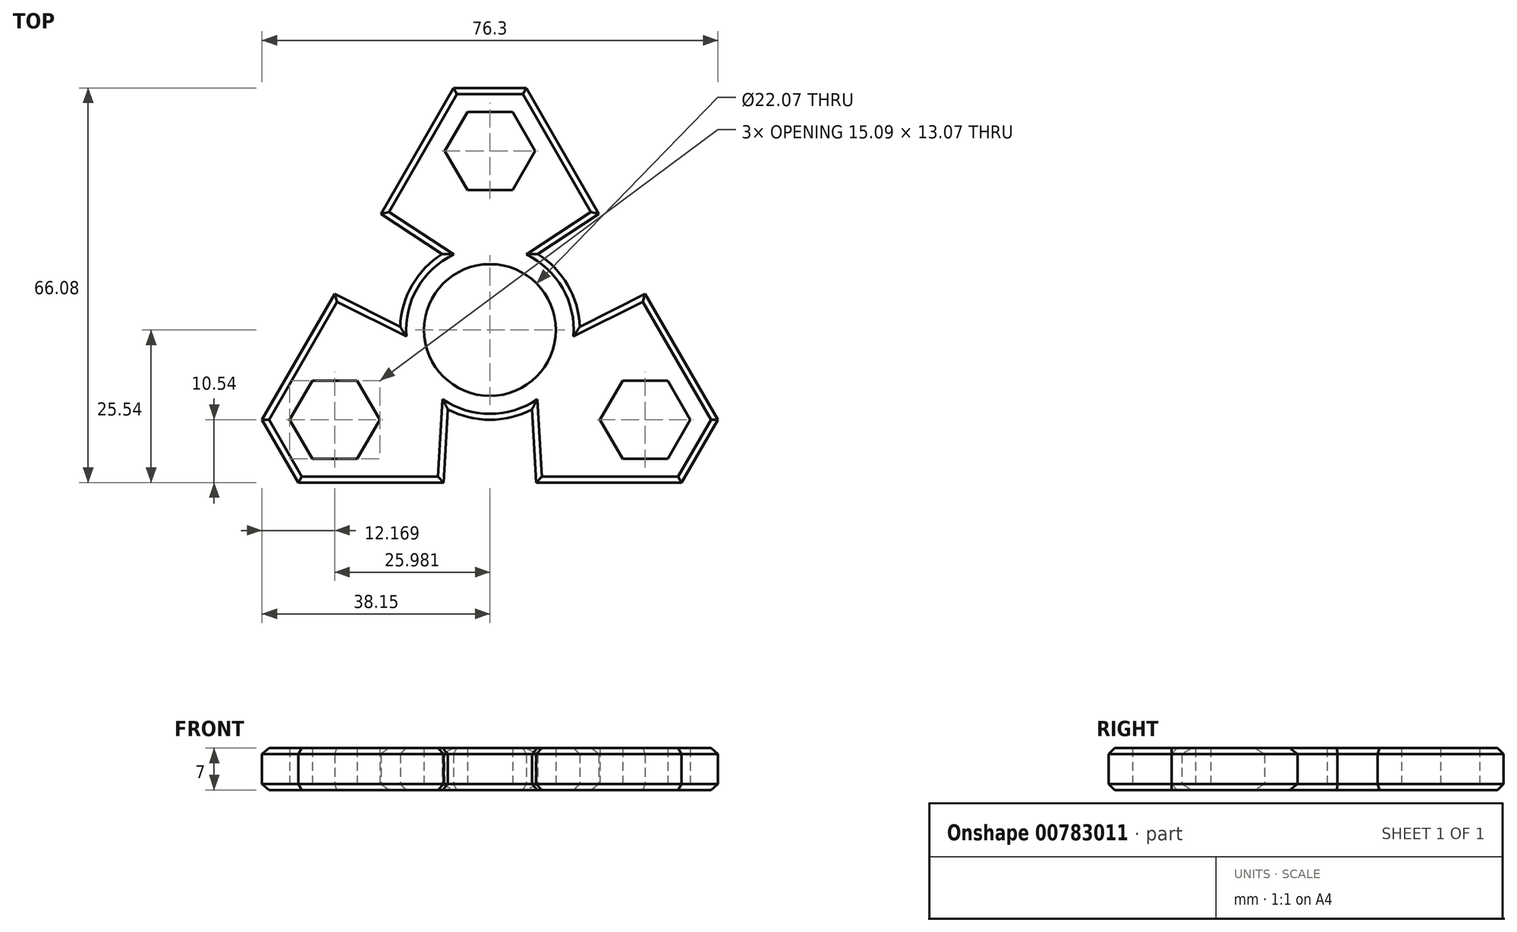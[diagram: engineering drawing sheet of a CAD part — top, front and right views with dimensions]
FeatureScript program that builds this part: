
annotation { "Feature Type Name" : "Feature", "Feature Type Description" : "" }
export const myFeature = defineFeature(function(context is Context, id is Id, definition is map)
    precondition{}
    {
        {
            var Q0;
            Q0=qCreatedBy(makeId("Top.planeOp"),FACE);
            var sketch = newSketch(context, id + "F0", { "sketchPlane" : qUnion([Q0])});
            skCircle(sketch, "E0", {"center": v(0, 0) * mm, "radius": 11.04 * mm});
            skCircle(sketch, "E1", {"center": v(0, 0) * mm, "radius": 15.04 * mm});
            skLineSegment(sketch, "E2", {"start": v(0, 0) * mm, "end": v(0, 79.85) * mm, "construction": true});
            skCircle(sketch, "E3.cCircle", {"center": v(0, 30) * mm, "radius": 6.53 * mm, "construction": true});
            skLineSegment(sketch, "E3.0", {"start": v(3.77, 23.46) * mm, "end": v(-3.77, 23.46) * mm});
            skLineSegment(sketch, "E3.1", {"start": v(-3.77, 23.46) * mm, "end": v(-7.55, 30) * mm});
            skLineSegment(sketch, "E3.2", {"start": v(-7.55, 30) * mm, "end": v(-3.77, 36.53) * mm});
            skLineSegment(sketch, "E3.3", {"start": v(-3.77, 36.53) * mm, "end": v(3.77, 36.53) * mm});
            skLineSegment(sketch, "E3.4", {"start": v(3.77, 36.53) * mm, "end": v(7.55, 30) * mm});
            skLineSegment(sketch, "E3.5", {"start": v(7.55, 30) * mm, "end": v(3.77, 23.46) * mm});
            skPoint(sketch, "E3.0.midPoint", {"position": v(0, 23.46) * mm});
            skCircle(sketch, "E4.cCircle", {"center": v(0, 30) * mm, "radius": 10.54 * mm, "construction": true});
            skLineSegment(sketch, "E4.0", {"start": v(6.08, 19.46) * mm, "end": v(-6.08, 19.46) * mm});
            skLineSegment(sketch, "E4.1", {"start": v(-6.08, 19.46) * mm, "end": v(-12.16, 30) * mm});
            skLineSegment(sketch, "E4.2", {"start": v(-12.16, 30) * mm, "end": v(-6.08, 40.53) * mm});
            skLineSegment(sketch, "E4.3", {"start": v(-6.08, 40.53) * mm, "end": v(6.08, 40.53) * mm});
            skLineSegment(sketch, "E4.4", {"start": v(6.08, 40.54) * mm, "end": v(12.16, 30) * mm});
            skLineSegment(sketch, "E4.5", {"start": v(12.16, 30) * mm, "end": v(6.08, 19.46) * mm});
            skPoint(sketch, "E4.0.midPoint", {"position": v(0, 19.46) * mm});
            skLineSegment(sketch, "E5", {"start": v(12.16, 30) * mm, "end": v(18.25, 19.46) * mm});
            skLineSegment(sketch, "E6", {"start": v(18.25, 19.47) * mm, "end": v(8, 12.73) * mm});
            skLineSegment(sketch, "E7", {"start": v(-12.16, 30) * mm, "end": v(-18.25, 19.46) * mm});
            skLineSegment(sketch, "E8", {"start": v(-18.25, 19.46) * mm, "end": v(-8, 12.73) * mm});
            skCircle(sketch, "E9", {"center": v(0, 0) * mm, "radius": 40.99 * mm, "construction": true});
            skLineSegment(sketch, "E10", {"start": v(0, 12.73) * mm, "end": v(8, 12.73) * mm, "construction": true});
            skLineSegment(sketch, "E11", {"start": v(0, 12.73) * mm, "end": v(-8, 12.73) * mm, "construction": true});
            skSolve(sketch);
        }
        {
            var Q0;
            Q0=qCreatedBy(makeId("Right.planeOp"),FACE);
            var sketch = newSketch(context, id + "F1", { "sketchPlane" : qUnion([Q0])});
            skLineSegment(sketch, "E12", {"start": v(0, 0) * mm, "end": v(0, 65.4) * mm, "construction": true});
            skSolve(sketch);
        }
        {
            var Q0;
            Q0=makeQuery(id+"F0.imprint","IMPRINT",FACE,{"disambiguationData":[TD([[makeQuery(id+"F0.imprint","IMPRINT",EDGE,{"derivedFrom":sQuery(id+"F0.wireOp",EDGE,"E0")}),-1.0]])]});
            var Q1;
            Q1=makeQuery(id+"F0.imprint","IMPRINT",FACE,{"disambiguationData":[TD([[makeQuery(id+"F0.imprint","IMPRINT",EDGE,{"derivedFrom":sQuery(id+"F0.wireOp",EDGE,"E3.0")}),1.0]])]});
            var Q2;
            Q2=makeQuery(id+"F0.imprint","IMPRINT",FACE,{"disambiguationData":[TD([[makeQuery(id+"F0.imprint","IMPRINT",EDGE,{"derivedFrom":sQuery(id+"F0.wireOp",EDGE,"E4.0")}),1.0]])]});
            var Q3;
            Q3=makeQuery(id+"F0.imprint","IMPRINT",FACE,{"disambiguationData":[TD([[makeQuery(id+"F0.imprint","IMPRINT",EDGE,{"derivedFrom":sQuery(id+"F0.wireOp",EDGE,"E4.2")}),1.0]])]});
            extrude(context, id + "F2", {"entities" : qUnion([Q0, Q1, Q2, Q3]), "depth" : 7 * mm, "offsetDistance" : 25 * mm});
        }
        {
            var Q0;
            Q0=makeQuery(id+"F2.opExtrude","CAP_EDGE",EDGE,{"disambiguationData":[OSD([sQuery(id+"F0.wireOp",EDGE,"E4.4"),sQuery(id+"F0.wireOp",EDGE,"E5")])],"isStart":false});
            var Q1;
            Q1=makeQuery(id+"F2.opExtrude","CAP_EDGE",EDGE,{"disambiguationData":[OSD([sQuery(id+"F0.wireOp",EDGE,"E4.3")])],"isStart":false});
            var Q2;
            Q2=makeQuery(id+"F2.opExtrude","CAP_EDGE",EDGE,{"disambiguationData":[OSD([sQuery(id+"F0.wireOp",EDGE,"E4.2"),sQuery(id+"F0.wireOp",EDGE,"E7")])],"isStart":true});
            var Q3;
            Q3=makeQuery(id+"F2.opExtrude","CAP_EDGE",EDGE,{"disambiguationData":[OSD([sQuery(id+"F0.wireOp",EDGE,"E6")])],"isStart":false});
            var Q4;
            Q4=makeQuery(id+"F2.opExtrude","CAP_EDGE",EDGE,{"disambiguationData":[OSD([sQuery(id+"F0.wireOp",EDGE,"E8")])],"isStart":false});
            var Q5;
            Q5=makeQuery(id+"F2.opExtrude","CAP_EDGE",EDGE,{"disambiguationData":[OSD([sQuery(id+"F0.wireOp",EDGE,"E6")])],"isStart":true});
            var Q6;
            Q6=makeQuery(id+"F2.opExtrude","CAP_EDGE",EDGE,{"disambiguationData":[OSD([sQuery(id+"F0.wireOp",EDGE,"E4.4"),sQuery(id+"F0.wireOp",EDGE,"E5")])],"isStart":true});
            var Q7;
            Q7=makeQuery(id+"F2.opExtrude","CAP_EDGE",EDGE,{"disambiguationData":[OSD([sQuery(id+"F0.wireOp",EDGE,"E4.3")])],"isStart":true});
            var Q8;
            Q8=makeQuery(id+"F2.opExtrude","CAP_EDGE",EDGE,{"disambiguationData":[OSD([sQuery(id+"F0.wireOp",EDGE,"E4.2"),sQuery(id+"F0.wireOp",EDGE,"E7")])],"isStart":false});
            var Q9;
            Q9=makeQuery(id+"F2.opExtrude","CAP_EDGE",EDGE,{"disambiguationData":[OSD([sQuery(id+"F0.wireOp",EDGE,"E1")])],"isStart":true});
            var Q10;
            Q10=makeQuery(id+"F2.opExtrude","CAP_EDGE",EDGE,{"disambiguationData":[OSD([sQuery(id+"F0.wireOp",EDGE,"E1")])],"isStart":false});
            var Q11;
            Q11=makeQuery(id+"F2.opExtrude","CAP_EDGE",EDGE,{"disambiguationData":[OSD([sQuery(id+"F0.wireOp",EDGE,"E8")])],"isStart":true});
            chamfer(context, id + "F3", {"entities" : qUnion([Q0, Q1, Q2, Q3, Q4, Q5, Q6, Q7, Q8, Q9, Q10, Q11]), "width" : 1 * mm, "tangentPropagation" : true});
        }
        {
            var Q0;
            Q0=makeQuery(id+"F2.opExtrude","SWEPT_BODY",BODY,{"disambiguationData":[OSD([sQuery(id+"F0.wireOp",EDGE,"E0"),sQuery(id+"F0.wireOp",EDGE,"E1"),sQuery(id+"F0.wireOp",EDGE,"E3.0"),sQuery(id+"F0.wireOp",EDGE,"E3.1"),sQuery(id+"F0.wireOp",EDGE,"E3.2"),sQuery(id+"F0.wireOp",EDGE,"E3.3"),sQuery(id+"F0.wireOp",EDGE,"E3.4"),sQuery(id+"F0.wireOp",EDGE,"E3.5"),sQuery(id+"F0.wireOp",EDGE,"E4.2"),sQuery(id+"F0.wireOp",EDGE,"E4.3"),sQuery(id+"F0.wireOp",EDGE,"E4.4"),sQuery(id+"F0.wireOp",EDGE,"E5"),sQuery(id+"F0.wireOp",EDGE,"E6"),sQuery(id+"F0.wireOp",EDGE,"E7"),sQuery(id+"F0.wireOp",EDGE,"E8")])]});
            var Q1;
            Q1=sQuery(id+"F1.wireOp",EDGE,"E12");
            circularPattern(context, id + "F4", {"operationType" : NewBodyOperationType.ADD, "entities" : qUnion([Q0]), "axis" : qUnion([Q1]), "angle" : 360 * degree, "instanceCount" : 3, "equalSpace" : true});
        }
    });
